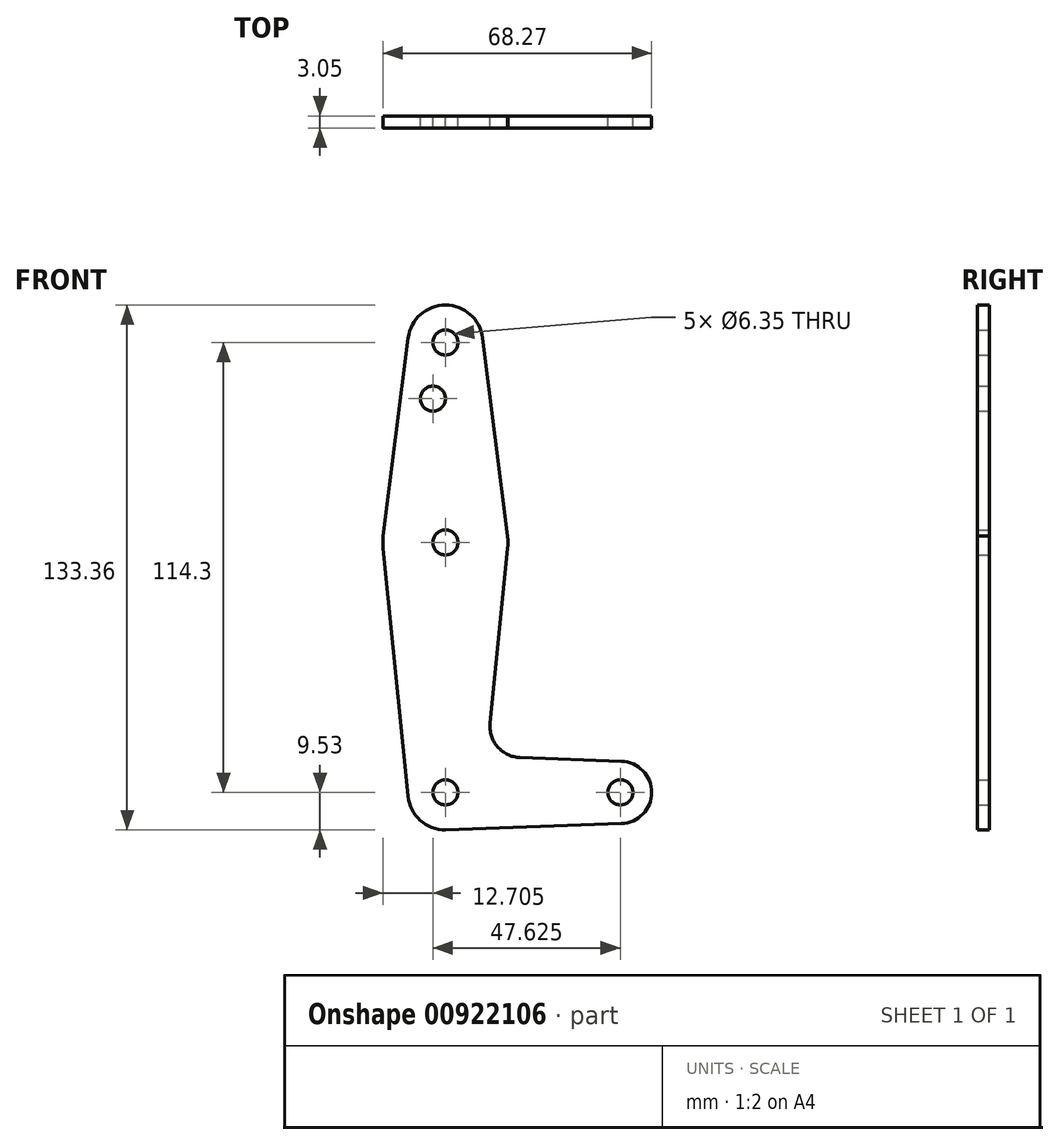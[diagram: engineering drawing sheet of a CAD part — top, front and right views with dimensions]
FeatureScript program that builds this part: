
annotation { "Feature Type Name" : "Feature", "Feature Type Description" : "" }
export const myFeature = defineFeature(function(context is Context, id is Id, definition is map)
    precondition{}
    {
        {
            var Q0;
            Q0=qCreatedBy(makeId("Front.planeOp"),FACE);
            var sketch = newSketch(context, id + "F0", { "sketchPlane" : qUnion([Q0])});
            skLineSegment(sketch, "E0", {"start": v(0, 0) * mm, "end": v(0, 114.3) * mm, "construction": true});
            skLineSegment(sketch, "E1", {"start": v(0, 0) * mm, "end": v(44.45, 0) * mm, "construction": true});
            skCircle(sketch, "E2", {"center": v(0, 114.3) * mm, "radius": 9.53 * mm});
            skCircle(sketch, "E3", {"center": v(0, 63.5) * mm, "radius": 15.88 * mm});
            skCircle(sketch, "E4", {"center": v(0, 0) * mm, "radius": 9.53 * mm});
            skCircle(sketch, "E5", {"center": v(44.45, 0) * mm, "radius": 7.94 * mm});
            skLineSegment(sketch, "E6", {"start": v(-9.45, 115.49) * mm, "end": v(-15.8, 65.09) * mm});
            skLineSegment(sketch, "E7", {"start": v(-15.8, 61.91) * mm, "end": v(-9.48, -0.95) * mm});
            skLineSegment(sketch, "E8", {"start": v(15.8, 65.09) * mm, "end": v(9.45, 115.49) * mm});
            skLineSegment(sketch, "E9", {"start": v(15.8, 61.91) * mm, "end": v(11.34, 17.6) * mm});
            skLineSegment(sketch, "E10", {"start": v(18.97, 8.85) * mm, "end": v(44.73, 7.93) * mm});
            skLineSegment(sketch, "E11", {"start": v(0, -9.53) * mm, "end": v(44.73, -7.93) * mm});
            skCircle(sketch, "E12", {"center": v(0, 63.5) * mm, "radius": 3.18 * mm});
            skCircle(sketch, "E13", {"center": v(0, 0) * mm, "radius": 3.18 * mm});
            skCircle(sketch, "E14", {"center": v(44.45, 0) * mm, "radius": 3.18 * mm});
            skArc(sketch, "E15.filletArc", {"start": v(11.34, 17.6) * mm, "mid": v(13.26, 11.57) * mm, "end": v(18.97, 8.85) * mm});
            skCircle(sketch, "E16", {"center": v(-3.18, 100.03) * mm, "radius": 3.18 * mm});
            skCircle(sketch, "E17", {"center": v(0, 114.3) * mm, "radius": 3.18 * mm});
            skSolve(sketch);
        }
        {
            var Q0;
            Q0=makeQuery(id+"F0.imprint","IMPRINT",FACE,{"disambiguationData":[TD([[makeQuery(id+"F0.imprint","IMPRINT",EDGE,{"derivedFrom":sQuery(id+"F0.wireOp",EDGE,"E17")}),-1.0]])]});
            var Q1;
            Q1=makeQuery(id+"F0.imprint","IMPRINT",FACE,{"disambiguationData":[TD([[makeQuery(id+"F0.imprint","IMPRINT",EDGE,{"derivedFrom":sQuery(id+"F0.wireOp",EDGE,"E16")}),-1.0]])]});
            var Q2;
            Q2=makeQuery(id+"F0.imprint","IMPRINT",FACE,{"disambiguationData":[TD([[makeQuery(id+"F0.imprint","IMPRINT",EDGE,{"derivedFrom":sQuery(id+"F0.wireOp",EDGE,"E12")}),-1.0]])]});
            var Q3;
            {var subQ0=sQuery(id+"F0.wireOp",EDGE,"E7");Q3=makeQuery(id+"F0.imprint","IMPRINT",FACE,{"disambiguationData":[TD([[makeQuery(id+"F0.imprint","IMPRINT",EDGE,{"derivedFrom":subQ0}),1.0]])]});}
            var Q4;
            Q4=makeQuery(id+"F0.imprint","IMPRINT",FACE,{"disambiguationData":[TD([[makeQuery(id+"F0.imprint","IMPRINT",EDGE,{"derivedFrom":sQuery(id+"F0.wireOp",EDGE,"E14")}),-1.0]])]});
            var Q5;
            Q5=makeQuery(id+"F0.imprint","IMPRINT",FACE,{"disambiguationData":[TD([[makeQuery(id+"F0.imprint","IMPRINT",EDGE,{"derivedFrom":sQuery(id+"F0.wireOp",EDGE,"E13")}),-1.0]])]});
            extrude(context, id + "F1", {"entities" : qUnion([Q0, Q1, Q2, Q3, Q4, Q5]), "depth" : 3.05 * mm, "offsetDistance" : 25.4 * mm});
        }
    });
